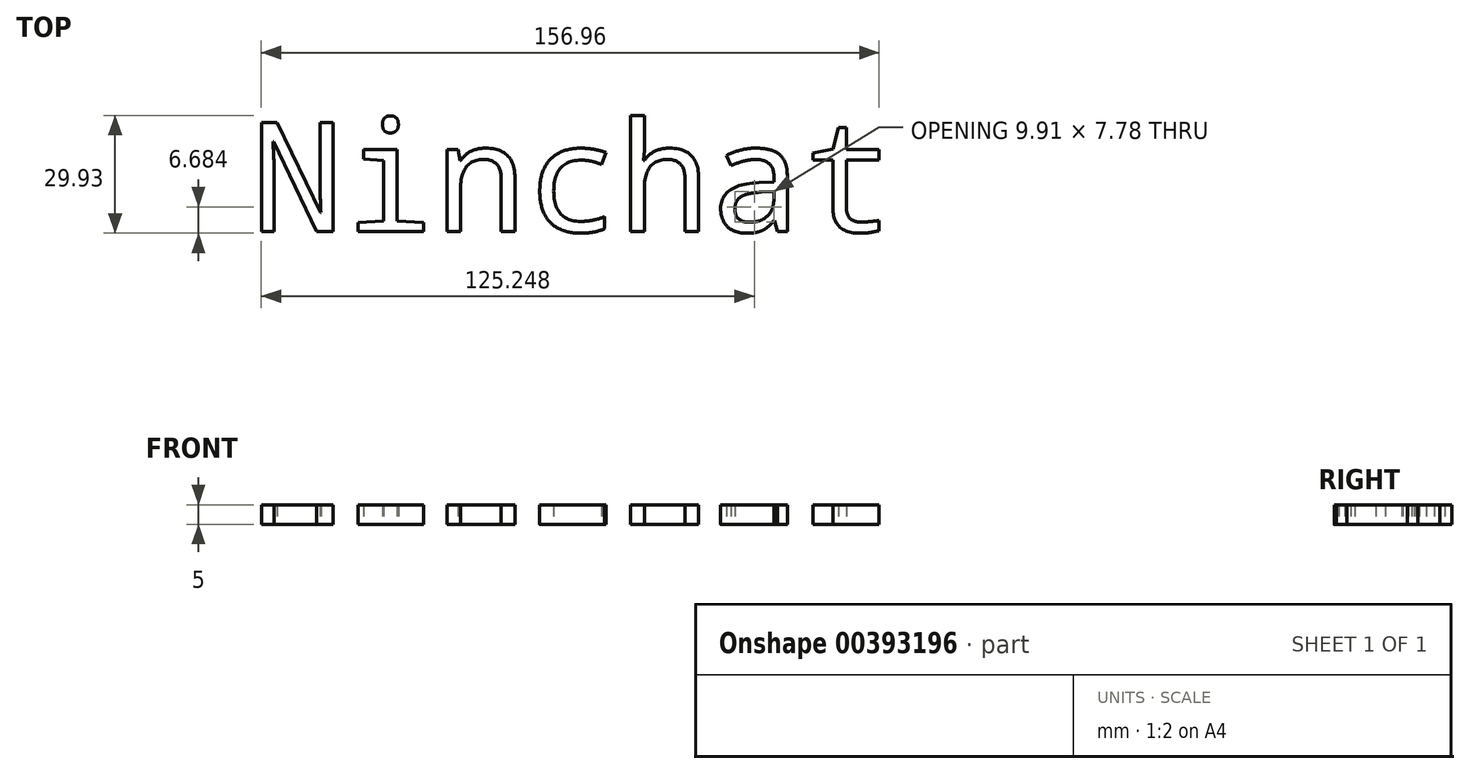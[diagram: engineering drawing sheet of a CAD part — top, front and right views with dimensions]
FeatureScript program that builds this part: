
annotation { "Feature Type Name" : "Feature", "Feature Type Description" : "" }
export const myFeature = defineFeature(function(context is Context, id is Id, definition is map)
    precondition{}
    {
        {
            var Q0;
            Q0=qCreatedBy(makeId("Top.planeOp"),FACE);
            var sketch = newSketch(context, id + "F0", { "sketchPlane" : qUnion([Q0])});
            skText(sketch, "E0", { "text": "Ninchat", "fontName": "DroidSansMono.ttf"});
            const initialGuessF0  = {"E0": [0, 0, 1, 0, 0.028]};
            skSetInitialGuess(sketch, initialGuessF0);
            skSolve(sketch);
        }
        {
            var Q0;
            Q0 = qSketchRegion(id + "F0", true);
            extrude(context, id + "F1", {"entities" : qUnion([Q0]), "depth" : 5 * mm});
        }
    });
